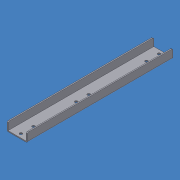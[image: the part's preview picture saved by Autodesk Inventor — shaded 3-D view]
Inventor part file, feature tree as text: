
AUTODESK INVENTOR PART (.ipt)
format: ipt  version: 2015 (Build 190159000, 159)  size: 188,416 bytes
history: native  units: mm
features: other x7, sheet_metal_op x5, sketch x5, plane x2, mirror x1, chamfer x1
ambient origin geometry x8: Origin, YZ Plane, XZ Plane, XY Plane, X Axis, Y Axis, Z Axis, Center Point
bodies: Solid1 (feature_tree)
feature tree (21):
  sheet_metal_op  "Face1"
  sheet_metal_op  "Flange1"
  sheet_metal_op  "Flange2"
  plane  "Work Plane1"
  mirror  "Mirror1"
  chamfer  "Corner Round1"
  plane  "Work Plane2"
  sketch  "Sketch1"  dims[d2=72.0mm]
  other  "Plate1"
  sketch  "Sketch2"  dims[d3=580.0mm]
  other  "Plate2"
  sheet_metal_op  "Bend1"
  sketch  "Sketch3"  dims[d4=0.001mm]
  other  "Plate3"
  sheet_metal_op  "Bend2"
  sketch  "Sketch4"  dims[d5=4.0mm]
  other  "FlatPattern"
  sketch  "Sketch5"  dims[d6=0.001mm d7=8.0mm d8=0.001mm d9=31.0mm d10=90.0deg d11=0.001mm d12=4.0mm d13=0.001mm d14=8.0mm d15=0.001mm d16=31.0mm d17=90.0deg d18=0.001mm d19=11.0mm d20=11.0mm d21=15.0mm d22=50.0mm d23=4.0mm d24=0.0mm d25=5.0mm d26=11.0mm d27=11.0mm d28=50.0mm d30=4.0mm d31=0.0mm d33=235.0mm d0=4.0mm]
  other  "Cut1"
  other  "Cut2"
  other  "FlatPatternExtrusion2"
